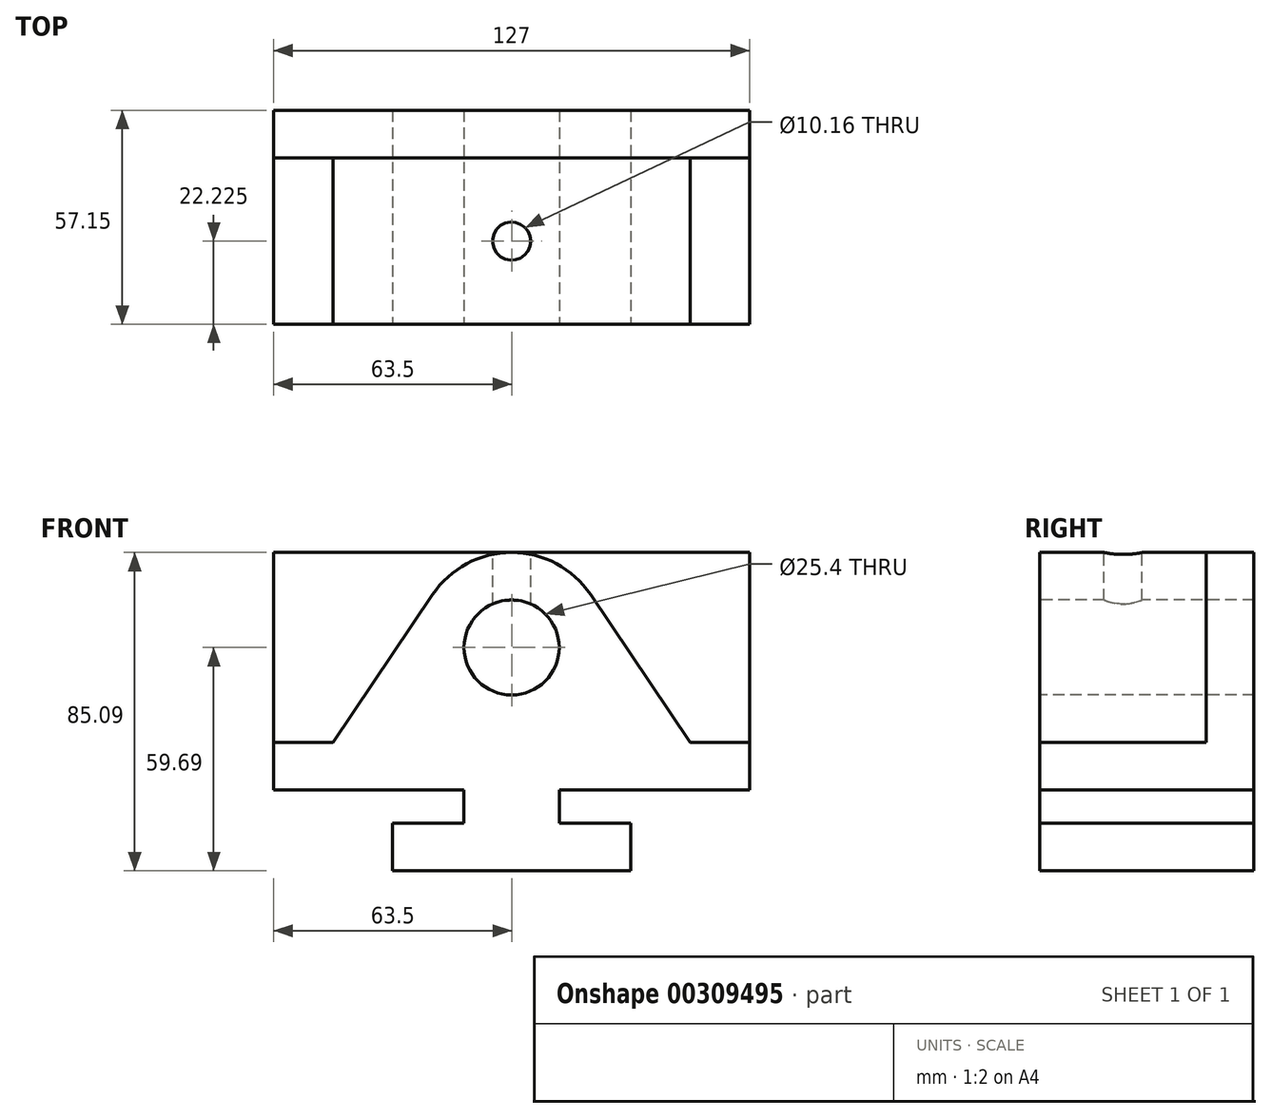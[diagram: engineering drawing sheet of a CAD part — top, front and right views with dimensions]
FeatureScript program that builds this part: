
annotation { "Feature Type Name" : "Feature", "Feature Type Description" : "" }
export const myFeature = defineFeature(function(context is Context, id is Id, definition is map)
    precondition{}
    {
        {
            var Q0;
            Q0=qCreatedBy(makeId("Front.planeOp"),FACE);
            var sketch = newSketch(context, id + "F0", { "sketchPlane" : qUnion([Q0])});
            skLineSegment(sketch, "E0", {"start": v(0, 0) * mm, "end": v(63.5, 0) * mm});
            skLineSegment(sketch, "E1", {"start": v(63.5, 0) * mm, "end": v(63.5, 12.7) * mm});
            skLineSegment(sketch, "E2", {"start": v(63.5, 12.7) * mm, "end": v(44.45, 12.7) * mm});
            skLineSegment(sketch, "E3", {"start": v(44.45, 12.7) * mm, "end": v(44.45, 21.59) * mm});
            skLineSegment(sketch, "E4", {"start": v(44.45, 21.6) * mm, "end": v(95.25, 21.6) * mm});
            skLineSegment(sketch, "E5", {"start": v(95.25, 21.59) * mm, "end": v(95.25, 34.3) * mm});
            skLineSegment(sketch, "E6", {"start": v(95.25, 34.3) * mm, "end": v(79.38, 34.3) * mm});
            skLineSegment(sketch, "E7", {"start": v(79.38, 34.3) * mm, "end": v(52.84, 73.84) * mm});
            skLineSegment(sketch, "E8", {"start": v(0, 0) * mm, "end": v(0, 12.7) * mm});
            skLineSegment(sketch, "E9", {"start": v(0, 12.7) * mm, "end": v(19.05, 12.7) * mm});
            skLineSegment(sketch, "E10", {"start": v(19.05, 12.7) * mm, "end": v(19.05, 21.59) * mm});
            skLineSegment(sketch, "E11", {"start": v(19.05, 21.59) * mm, "end": v(-31.75, 21.59) * mm});
            skLineSegment(sketch, "E12", {"start": v(-31.75, 21.59) * mm, "end": v(-31.75, 34.3) * mm});
            skLineSegment(sketch, "E13", {"start": v(-31.75, 34.3) * mm, "end": v(-15.88, 34.3) * mm});
            skLineSegment(sketch, "E14", {"start": v(-15.87, 34.29) * mm, "end": v(10.66, 73.84) * mm});
            skArc(sketch, "E15", {"start": v(52.84, 73.84) * mm, "mid": v(31.75, 85.1) * mm, "end": v(10.66, 73.84) * mm});
            skCircle(sketch, "E16", {"center": v(31.75, 59.69) * mm, "radius": 12.7 * mm});
            skLineSegment(sketch, "E17", {"start": v(-31.75, 34.3) * mm, "end": v(-31.75, 85.1) * mm});
            skPoint(sketch, "E17.endSnap0", {"position": v(31.75, 85.1) * mm});
            skLineSegment(sketch, "E18", {"start": v(-31.75, 85.1) * mm, "end": v(95.25, 85.09) * mm});
            skLineSegment(sketch, "E19", {"start": v(95.25, 85.09) * mm, "end": v(95.25, 34.3) * mm});
            skSolve(sketch);
        }
        {
            var Q0;
            Q0 = qSketchRegion(id + "F0", true);
            extrude(context, id + "F1", {"entities" : qUnion([Q0]), "oppositeDirection" : true, "depth" : 57.15 * mm});
        }
        {
            var Q0;
            Q0=makeQuery(id+"F0.imprint","IMPRINT",FACE,{"disambiguationData":[TD([[makeQuery(id+"F0.imprint","IMPRINT",EDGE,{"derivedFrom":sQuery(id+"F0.wireOp",EDGE,"E6")}),-1.0]])]});
            var Q1;
            Q1=makeQuery(id+"F0.imprint","IMPRINT",FACE,{"disambiguationData":[TD([[makeQuery(id+"F0.imprint","IMPRINT",EDGE,{"derivedFrom":sQuery(id+"F0.wireOp",EDGE,"E13")}),1.0]])]});
            extrude(context, id + "F2", {"entities" : qUnion([Q0, Q1]), "operationType" : NewBodyOperationType.REMOVE, "oppositeDirection" : true, "depth" : 44.45 * mm});
        }
        {
            var Q0;
            Q0=makeQuery(id+"F1.opExtrude","SWEPT_FACE",FACE,{"disambiguationData":[OSD([sQuery(id+"F0.wireOp",EDGE,"E18")])]});
            var sketch = newSketch(context, id + "F3", { "sketchPlane" : qUnion([Q0])});
            skCircle(sketch, "E20", {"center": v(31.75, 22.22) * mm, "radius": 5.08 * mm});
            skSolve(sketch);
        }
        {
            var Q0;
            Q0=makeQuery(id+"F3.imprint","IMPRINT",FACE,{"disambiguationData":[TD([[makeQuery(id+"F3.imprint","IMPRINT",EDGE,{"derivedFrom":sQuery(id+"F3.wireOp",EDGE,"E20")}),1.0]])]});
            extrude(context, id + "F4", {"entities" : qUnion([Q0]), "operationType" : NewBodyOperationType.REMOVE, "oppositeDirection" : true, "depth" : 25.4 * mm});
        }
    });
